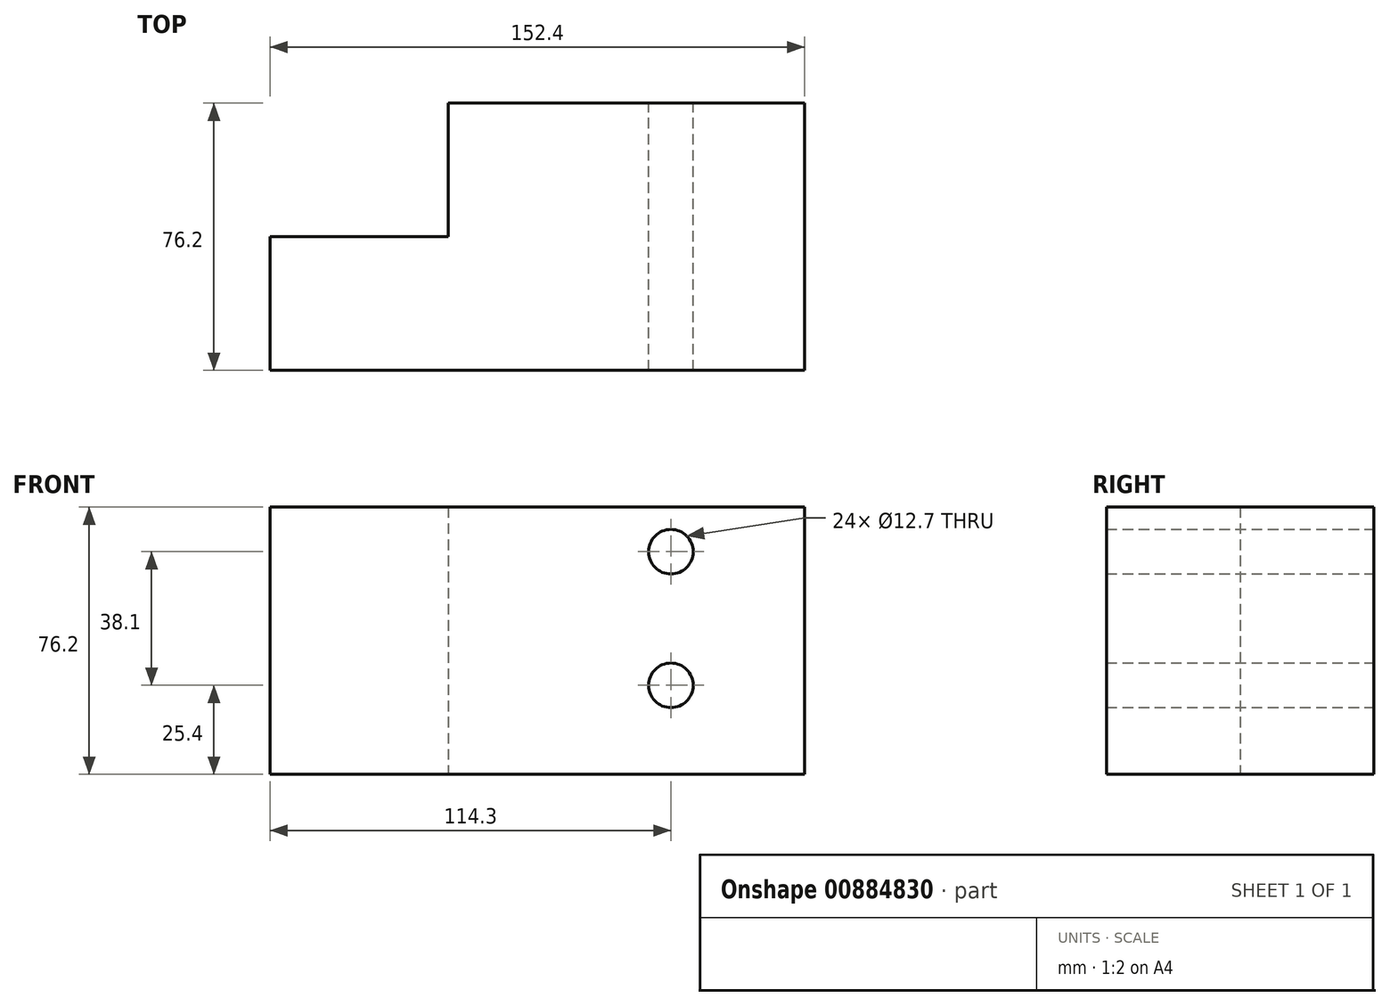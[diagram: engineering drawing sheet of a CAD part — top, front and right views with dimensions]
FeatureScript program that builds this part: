
annotation { "Feature Type Name" : "Feature", "Feature Type Description" : "" }
export const myFeature = defineFeature(function(context is Context, id is Id, definition is map)
    precondition{}
    {
        {
            var Q0;
            Q0=qCreatedBy(makeId("Top.planeOp"),FACE);
            var sketch = newSketch(context, id + "F0", { "sketchPlane" : qUnion([Q0])});
            skLineSegment(sketch, "E0.bottom", {"start": v(76.2, 15.04) * mm, "end": v(-76.2, 15.04) * mm});
            skLineSegment(sketch, "E0.top", {"start": v(76.2, -23.06) * mm, "end": v(-76.2, -23.06) * mm});
            skLineSegment(sketch, "E0.left", {"start": v(76.2, 15.04) * mm, "end": v(76.2, -23.06) * mm});
            skLineSegment(sketch, "E0.right", {"start": v(-76.2, 15.04) * mm, "end": v(-76.2, -23.06) * mm});
            skPoint(sketch, "E0.middle", {"position": v(0, -4.01) * mm});
            skLineSegment(sketch, "E1", {"start": v(-25.4, 15.04) * mm, "end": v(-25.4, 53.14) * mm});
            skLineSegment(sketch, "E2", {"start": v(-25.4, 53.14) * mm, "end": v(76.2, 53.14) * mm});
            skLineSegment(sketch, "E3", {"start": v(76.2, 53.14) * mm, "end": v(76.2, 15.04) * mm});
            skSolve(sketch);
        }
        {
            var Q0;
            Q0 = qSketchRegion(id + "F0", true);
            extrude(context, id + "F1", {"entities" : qUnion([Q0]), "depth" : 76.2 * mm, "offsetDistance" : 25.4 * mm});
        }
        {
            var Q0;
            Q0=makeQuery(id+"F1.opExtrude","SWEPT_FACE",FACE,{"disambiguationData":[OSD([sQuery(id+"F0.wireOp",EDGE,"E2")])]});
            var sketch = newSketch(context, id + "F2", { "sketchPlane" : qUnion([Q0])});
            skCircle(sketch, "E4", {"center": v(-38.1, 25.4) * mm, "radius": 6.35 * mm});
            skCircle(sketch, "E5", {"center": v(-38.1, 63.5) * mm, "radius": 6.35 * mm});
            skSolve(sketch);
        }
        {
            var Q0;
            Q0 = qSketchRegion(id + "F2", true);
            extrude(context, id + "F3", {"entities" : qUnion([Q0]), "operationType" : NewBodyOperationType.REMOVE, "oppositeDirection" : true, "depth" : 76.2 * mm, "offsetDistance" : 25.4 * mm});
        }
    });
